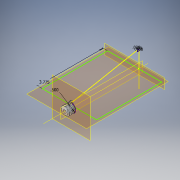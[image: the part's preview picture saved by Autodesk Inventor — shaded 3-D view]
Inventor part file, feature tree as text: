
AUTODESK INVENTOR PART (.ipt)
format: ipt  version: 2018 (Build 220112000, 112)  size: 553,472 bytes
history: native  units: in
note: dims shown in document units (in); Inventor stores cm internally (conversion verified against a paired STEP export)
features: sketch x8, extrude x4, helix x3, other x2, hole x2, plane x1, loft x1, projected_geometry x1
ambient origin geometry x8: Origin, YZ Plane, XZ Plane, XY Plane, X Axis, Y Axis, Z Axis, Center Point
bodies: Solid1 (feature_tree)
feature tree (22):
  sketch  "Sketch1"  dims[d0=2.0in d2=3.9in]
  plane  "Work Plane1"
  sketch  "Sketch2"  dims[d3=0.5in d5=0.0in d6=90.0deg d7=0.0in d8=90.0deg]
  loft  "Loft1"
  other  "Work Point1"
  hole  "Hole1"  [1 undecoded]
  other  "Work Axis2"
  sketch  "Sketch6"  dims[d61=1.0in d62=1.0in d11=0.18in d12=0.75in d13=0.375in d14=0.25in d15=0.5635in d16=1.0in d17=0.8108in d41=0.1in]
  helix  "Coil3"  [1 undecoded]
  helix  "Coil4"  [1 undecoded]
  sketch  "Sketch8"  dims[d42=0.1in d43=0.02in]
  extrude  "Extrusion2"  Depth=0.1in
  helix  "Coil5"  [1 undecoded]
  extrude  "Extrusion3"  Depth=0.1in
  extrude  "Extrusion4"  Depth=0.1in
  sketch  "Sketch12"  dims[d67=0.02in d68=0.1in d69=0.185in d70=0.13in d71=0.5436in d72=0.13in d73=1.0in d74=10.2362in d75=0.0in d76=90.0deg d77=90.0deg d78=0.0in d79=0.0in d80=0.37in d81=0.3in d82=0.0in d83=1.0in d84=0.0in d86=0.02in d87=0.0in d88=0.125in d89=3.0in d90=0.0in d91=0.0in d92=0.5in d93=1.0in d94=1.0in d95=0.18in d96=0.75in d97=0.375in d98=0.25in d99=0.5635in d100=1.0in d101=0.8108in d102=3.0in d103=0.0in]
  hole  "Hole2"  [1 undecoded]
  extrude  "Extrusion5"  Depth=0.13in
  projected_geometry  "Projected Loop1"
  sketch  "Sketch9"  dims[d44=0.13in d45=1.0in d46=11.811in d47=-0.0739in d48=90.0deg d49=90.0deg d50=0.0in d51=0.0in]
  sketch  "Sketch10"  dims[d52=0.13in d53=1.0in d54=11.811in d55=0.0756in d56=90.0deg d57=90.0deg d58=0.0in d59=0.0in d60=3.775in]
  sketch  "Sketch11"  dims[d63=3.25in d64=0.0in d66=0.1in]
note: 5 required parameter values undecoded (feature->parameter linkage not recoverable at this tier; creation-order binding heuristic only, values carry confidence <= 0.55)
